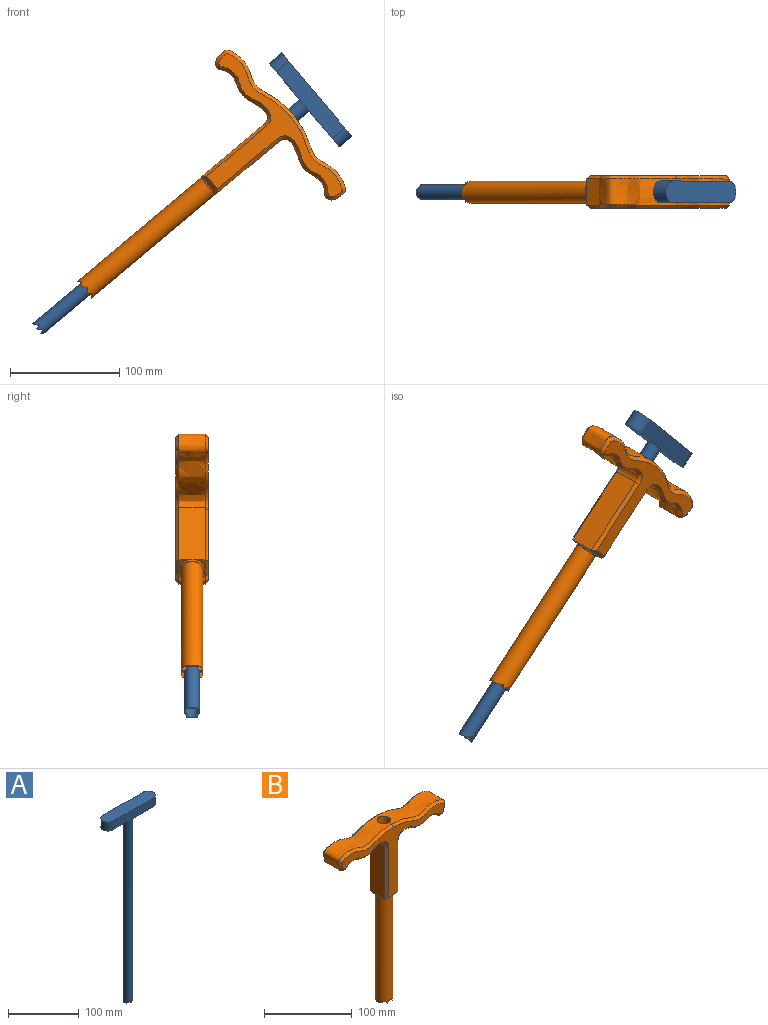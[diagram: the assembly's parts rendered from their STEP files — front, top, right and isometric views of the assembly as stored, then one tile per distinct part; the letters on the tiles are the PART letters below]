
ASSEMBLY  parts=2 mates=1
PART A: 21 faces, bbox 100x20x335 mm
  f0: cylinder r=7mm len=320mm, axis (0,0,1), area 14000.8mm2, adj f1,f2,f3,f4,f11,f13,f14,f15
  f1: plane 1.85x0.07mm, normal (0,0,-1), area 0.1mm2, adj f0,f5,f19,f20
  f2: plane 1.85x0.07mm, normal (0,0,-1), area 0.1mm2, adj f0,f5,f17,f20
  f3: plane 1.02x0.09mm, normal (0,0,-1), area 0.1mm2, adj f0,f5,f13,f18
  f4: plane 1.02x0.09mm, normal (0,0,-1), area 0.1mm2, adj f0,f5,f14,f16
  f5: cylinder r=6mm len=283.8mm, axis (0,0,-1), area 10633.1mm2, adj f1,f2,f3,f4,f12,f13,f14,f15
  f6: plane 80x15mm, normal (0,1,0), area 1200mm2, adj f7,f9,f10,f11
  f7: cylinder r=10mm len=20mm, axis (0,0,-1), area 471.2mm2, adj f6,f8,f10,f11
  f8: plane 80x15mm, normal (0,-1,0), area 1200mm2, adj f7,f9,f10,f11
  f9: cylinder r=10mm len=20mm, axis (0,0,-1), area 471.2mm2, adj f6,f8,f10,f11
  f10: plane 100x20mm, normal (0,0,1), area 1914.2mm2, adj f6,f7,f8,f9
  f11: plane 100x20mm, normal (0,0,-1), area 1760.2mm2, adj f0,f6,f7,f8,f9
  f12: plane 12x12mm, normal (0,0,-1), area 113.1mm2, adj f5
  f13: plane 4x1.16mm, normal (-0.99,0,-0.16), area 4.1mm2, adj f0,f3,f5,f15
  f14: plane 4x1.16mm, normal (-0.99,0,-0.16), area 4.1mm2, adj f0,f4,f5,f15
  f15: plane 13.65x5.45mm, normal (0.59,0,-0.81), area 21.4mm2, adj f0,f5,f13,f14
  f16: plane 4.59x4.11mm, normal (0.67,0,-0.74), area 6.5mm2, adj f0,f4,f5,f17
  f17: plane 4.11x2.98mm, normal (-0.94,0,-0.34), area 6.2mm2, adj f0,f2,f5,f16
  f18: plane 4.59x4.11mm, normal (0.67,0,-0.74), area 6.5mm2, adj f0,f3,f5,f19
  f19: plane 4.11x2.98mm, normal (-0.94,0,-0.34), area 6.2mm2, adj f0,f1,f5,f18
  f20: plane 9.12x2.42mm, normal (0.82,0,-0.57), area 13.9mm2, adj f0,f1,f2,f5
PART B: 36 faces, bbox 172.4x31.9x252 mm
  f0: plane 10.54x6.26mm, normal (0,0,-1), area 19mm2, adj f6,f14,f34
  f1: plane 10.54x6.26mm, normal (0,0,-1), area 19mm2, adj f9,f14,f34
  f2: plane 10.54x6.26mm, normal (0,0,-1), area 19mm2, adj f9,f19,f33
  f3: cylinder r=10mm len=147.89mm, axis (0,0,1), area 9201.1mm2, adj f22,f23,f24,f25,f26,f27,f28,f29
  f4: cylinder r=7.5mm len=249.51mm, axis (0,0,-1), area 11666mm2, adj f7,f8,f22,f23,f24,f25,f26,f27
  f5: plane 10.54x6.26mm, normal (0,0,-1), area 19mm2, adj f6,f19,f33
  f6: plane 74.57x24.19mm, normal (1,0,0), area 1785.2mm2, adj f0,f5,f7,f16,f21,f35
  f7: extruded ~85.22x25.62mm, area 4307mm2, adj f4,f6,f8,f15,f20
  f8: extruded ~85.22x25.62mm, area 4307mm2, adj f4,f7,f9,f13,f18
  f9: plane 74.57x24.19mm, normal (-1,0,0), area 1785.2mm2, adj f1,f2,f8,f12,f17,f32
  f10: plane 165.19x94.63mm, normal (0,-1,0), area 2957.4mm2, adj f17,f18,f19,f20,f21
  f11: plane 165.24x94.59mm, normal (0,1,0), area 3158.7mm2, adj f12,f13,f14,f15,f16
  f12: plane 74.62x3mm, normal (-0.71,0.71,0), area 309.7mm2, adj f9,f11,f13,f14
  f13: bspline ~90.05x29.94mm, area 769.7mm2, adj f8,f11,f12,f15
  f14: plane 21.07x3mm, normal (0,0.71,-0.71), area 76.7mm2, adj f0,f1,f11,f12,f16
  f15: bspline ~90.05x29.94mm, area 762.1mm2, adj f7,f11,f13,f16
  f16: plane 74.62x3mm, normal (0.71,0.71,0), area 309.7mm2, adj f6,f11,f14,f15
  f17: plane 74.62x3mm, normal (-0.71,-0.71,0), area 309.7mm2, adj f9,f10,f18,f19
  f18: bspline ~90.09x29.91mm, area 767.7mm2, adj f8,f10,f17,f20
  f19: plane 21.07x3mm, normal (0,-0.71,-0.71), area 76.7mm2, adj f2,f5,f10,f17,f21
  f20: bspline ~90.09x29.91mm, area 769.7mm2, adj f7,f10,f18,f21
  f21: plane 74.62x3mm, normal (0.71,-0.71,0), area 309.7mm2, adj f6,f10,f19,f20
  f22: plane 17.3x5.52mm, normal (0.64,0,-0.77), area 42.8mm2, adj f3,f4,f30,f31
  f23: plane 17.3x5.52mm, normal (-0.64,0,-0.77), area 42.8mm2, adj f3,f4,f24,f25
  f24: plane 5.44x2.96mm, normal (0.77,0,-0.64), area 11.1mm2, adj f3,f4,f23,f27
  f25: plane 5.44x2.96mm, normal (0.77,0,-0.64), area 11.1mm2, adj f3,f4,f23,f26
  f26: plane 4.3x3.9mm, normal (-0.64,0,-0.77), area 14.1mm2, adj f3,f4,f25,f28
  f27: plane 4.3x3.9mm, normal (-0.64,0,-0.77), area 14.1mm2, adj f3,f4,f24,f29
  f28: plane 4.3x3.9mm, normal (0.64,0,-0.77), area 14.1mm2, adj f3,f4,f26,f31
  f29: plane 4.3x3.9mm, normal (0.64,0,-0.77), area 14.1mm2, adj f3,f4,f27,f30
  f30: plane 5.44x2.96mm, normal (-0.77,0,-0.64), area 11.1mm2, adj f3,f4,f22,f29
  f31: plane 5.44x2.96mm, normal (-0.77,0,-0.64), area 11.1mm2, adj f3,f4,f22,f28
  f32: bspline ~12.25x2.21mm, area 21.6mm2, adj f3,f9,f33,f34
  f33: torus R=12mm, axis (0,0,-1), area 72.2mm2, adj f2,f3,f5,f32,f35
  f34: torus R=12mm, axis (0,0,-1), area 72.2mm2, adj f0,f1,f3,f32,f35
  f35: bspline ~12.25x2.21mm, area 21.6mm2, adj f3,f6,f33,f34
PLACE A rot(axis=(0,1,0),50deg) t=(-264.57,-51.87,235.53)mm
PLACE B rot(axis=(0,1,0),50deg) t=(-351.48,-36.87,162.6)mm
MATE cylindrical A.f0 <-> B.f3  axis (0.77,0,0.64) through (-387.14,-51.87,132.68)mm
